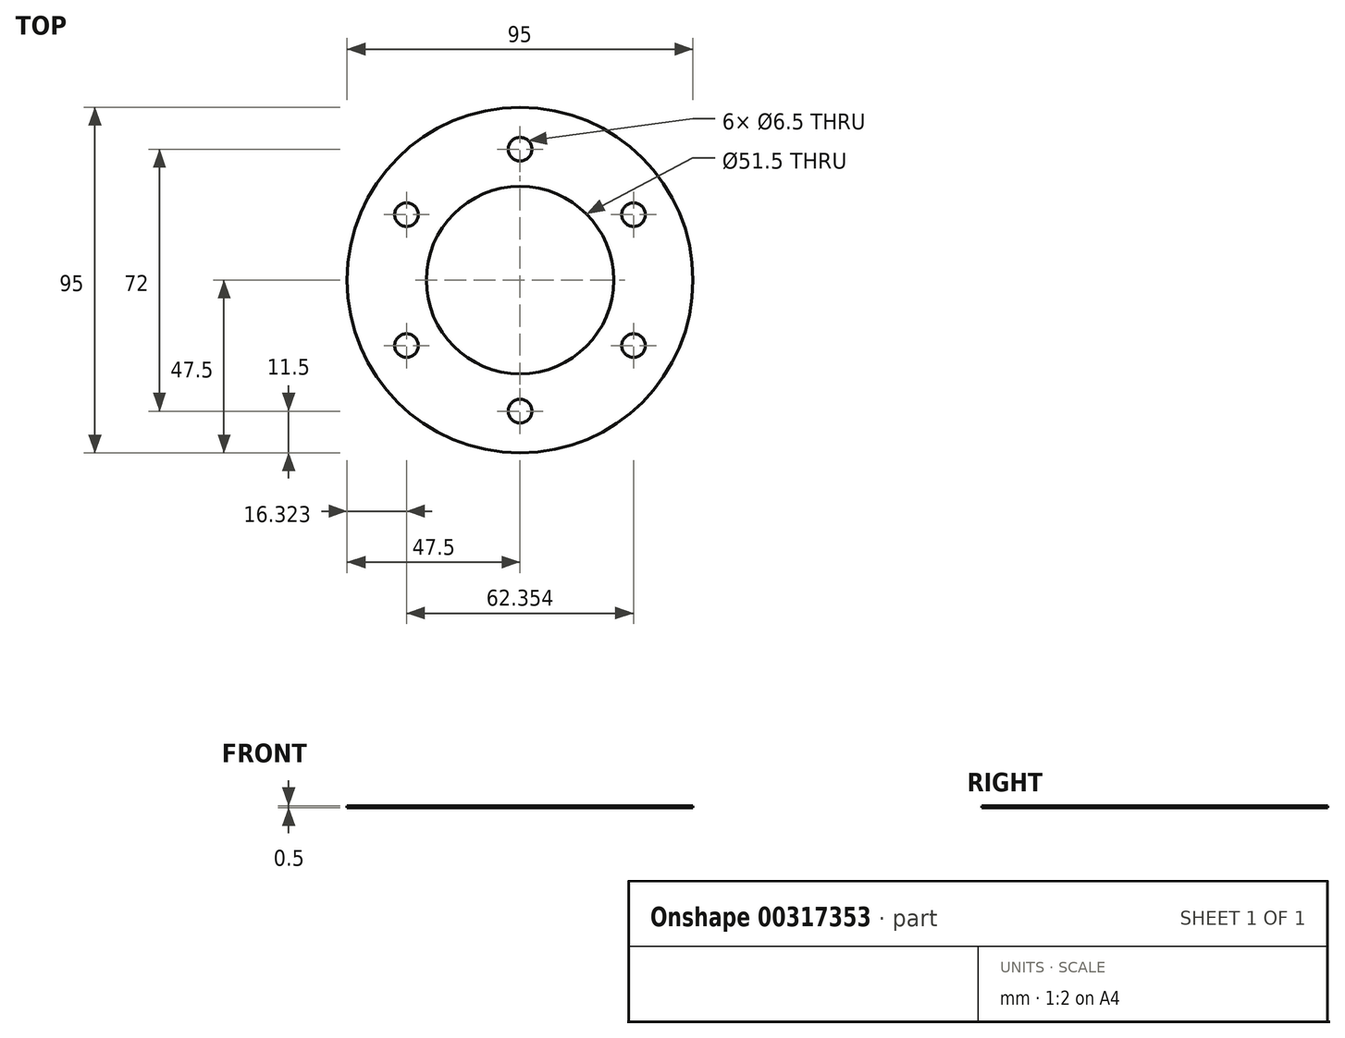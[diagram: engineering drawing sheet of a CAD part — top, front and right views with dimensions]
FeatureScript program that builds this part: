
annotation { "Feature Type Name" : "Feature", "Feature Type Description" : "" }
export const myFeature = defineFeature(function(context is Context, id is Id, definition is map)
    precondition{}
    {
        {
            var Q0;
            Q0=qCreatedBy(makeId("Top.planeOp"),FACE);
            var sketch = newSketch(context, id + "F0", { "sketchPlane" : qUnion([Q0])});
            skCircle(sketch, "E0", {"center": v(0, 0) * mm, "radius": 47.5 * mm});
            skCircle(sketch, "E1", {"center": v(0, 0) * mm, "radius": 25.75 * mm});
            skCircle(sketch, "E2", {"center": v(0, 36) * mm, "radius": 3.25 * mm});
            skCircle(sketch, "E3.1.0", {"center": v(-31.18, 18) * mm, "radius": 3.25 * mm});
            skCircle(sketch, "E3.2.0", {"center": v(-31.18, -18) * mm, "radius": 3.25 * mm});
            skCircle(sketch, "E3.3.0", {"center": v(0, -36) * mm, "radius": 3.25 * mm});
            skCircle(sketch, "E3.4.0", {"center": v(31.18, -18) * mm, "radius": 3.25 * mm});
            skCircle(sketch, "E3.5.0", {"center": v(31.18, 18) * mm, "radius": 3.25 * mm});
            skSolve(sketch);
        }
        {
            var Q0;
            Q0=makeQuery(id+"F0.imprint","IMPRINT",FACE,{"disambiguationData":[TD([[makeQuery(id+"F0.imprint","IMPRINT",EDGE,{"derivedFrom":sQuery(id+"F0.wireOp",EDGE,"E0")}),1.0]])]});
            extrude(context, id + "F1", {"entities" : qUnion([Q0]), "depth" : 0.5 * mm});
        }
    });
